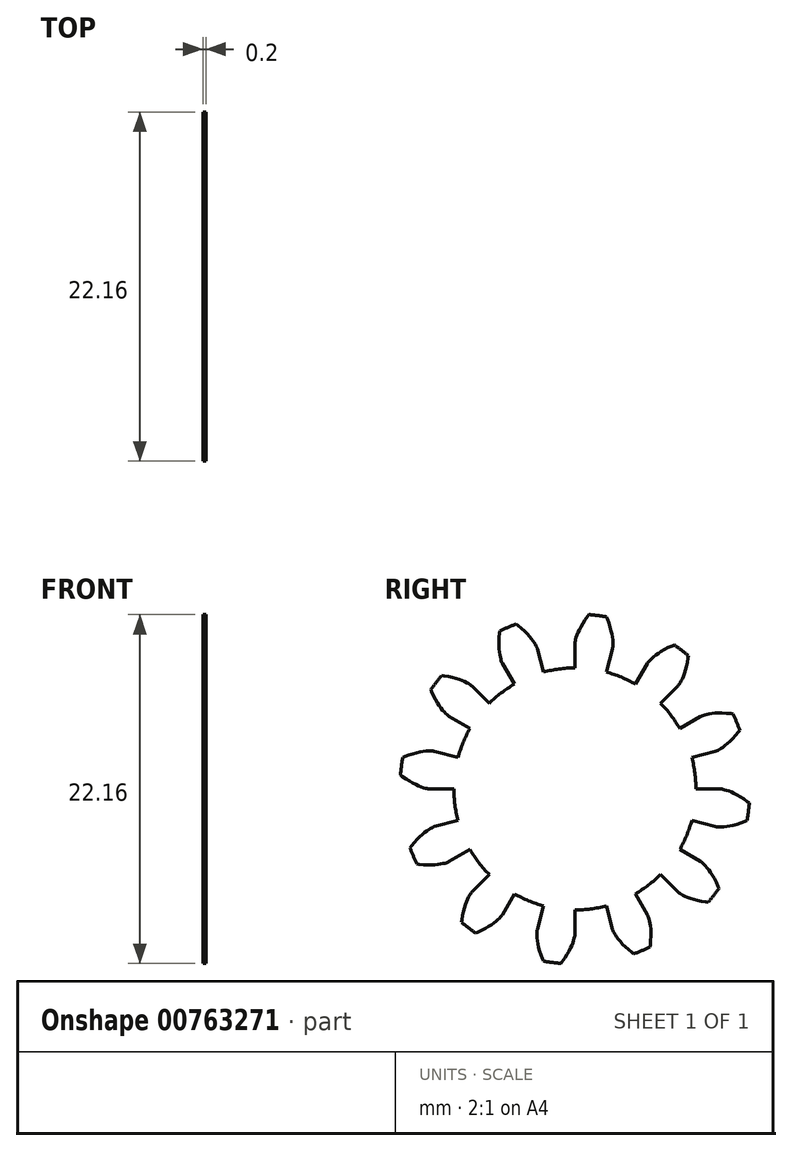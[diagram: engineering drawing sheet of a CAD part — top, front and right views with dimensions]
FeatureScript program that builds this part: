
annotation { "Feature Type Name" : "Feature", "Feature Type Description" : "" }
export const myFeature = defineFeature(function(context is Context, id is Id, definition is map)
    precondition{}
    {
        {
            assignVariable(context, id + "F0", {"name" : "GearThickness", "anyValue" : .196});
        }
        {
            var Q0;
            Q0=qCreatedBy(makeId("Right.planeOp"),FACE);
            var sketch = newSketch(context, id + "F1", { "sketchPlane" : qUnion([Q0])});
            skCircle(sketch, "E0", {"center": v(0, 0) * mm, "radius": 7.69 * mm});
            skCircle(sketch, "E1", {"center": v(0, 0) * mm, "radius": 9.22 * mm, "construction": true});
            skCircle(sketch, "E2", {"center": v(0, 0) * mm, "radius": 9.53 * mm, "construction": true});
            skCircle(sketch, "E3", {"center": v(0, 0) * mm, "radius": 11.11 * mm});
            skLineSegment(sketch, "E4", {"start": v(0, 0) * mm, "end": v(-9.22, 0) * mm, "construction": true});
            skLineSegment(sketch, "E5.1.0", {"start": v(0, 0) * mm, "end": v(-9.21, 0.46) * mm, "construction": true});
            skLineSegment(sketch, "E5.2.0", {"start": v(0, 0) * mm, "end": v(-9.18, 0.92) * mm, "construction": true});
            skLineSegment(sketch, "E5.3.0", {"start": v(0, 0) * mm, "end": v(-9.12, 1.38) * mm, "construction": true});
            skLineSegment(sketch, "E5.4.0", {"start": v(0, 0) * mm, "end": v(-9.04, 1.83) * mm, "construction": true});
            skLineSegment(sketch, "E5.5.0", {"start": v(0, 0) * mm, "end": v(-8.93, 2.28) * mm, "construction": true});
            skLineSegment(sketch, "E5.6.0", {"start": v(0, 0) * mm, "end": v(-8.8, 2.73) * mm, "construction": true});
            skLineSegment(sketch, "E5.7.0", {"start": v(0, 0) * mm, "end": v(-8.66, 3.16) * mm, "construction": true});
            skLineSegment(sketch, "E5.8.0", {"start": v(0, 0) * mm, "end": v(-8.5, 3.6) * mm, "construction": true});
            skLineSegment(sketch, "E5.9.0", {"start": v(0, 0) * mm, "end": v(-8.3, 4.01) * mm, "construction": true});
            skLineSegment(sketch, "E5.10.0", {"start": v(0, 0) * mm, "end": v(-8.1, 4.42) * mm, "construction": true});
            skLineSegment(sketch, "E5.11.0", {"start": v(0, 0) * mm, "end": v(-7.86, 4.82) * mm, "construction": true});
            skLineSegment(sketch, "E5.12.0", {"start": v(0, 0) * mm, "end": v(-7.61, 5.2) * mm, "construction": true});
            skLineSegment(sketch, "E5.13.0", {"start": v(0, 0) * mm, "end": v(-7.34, 5.58) * mm, "construction": true});
            skLineSegment(sketch, "E5.14.0", {"start": v(0, 0) * mm, "end": v(-7.05, 5.94) * mm, "construction": true});
            skLineSegment(sketch, "E5.anchor2", {"start": v(0, 0) * mm, "end": v(-7.05, 5.94) * mm, "construction": true});
            skLineSegment(sketch, "E6", {"start": v(-9.21, 0.46) * mm, "end": v(-9.23, 0) * mm, "construction": true});
            skLineSegment(sketch, "E7", {"start": v(-9.18, 0.92) * mm, "end": v(-9.27, 0) * mm, "construction": true});
            skLineSegment(sketch, "E8", {"start": v(-9.12, 1.38) * mm, "end": v(-9.32, 0.01) * mm, "construction": true});
            skLineSegment(sketch, "E9", {"start": v(-8.93, 2.28) * mm, "end": v(-9.5, 0.05) * mm, "construction": true});
            skLineSegment(sketch, "E10", {"start": v(-8.8, 2.73) * mm, "end": v(-9.63, 0.08) * mm, "construction": true});
            skLineSegment(sketch, "E11", {"start": v(-8.66, 3.16) * mm, "end": v(-9.77, 0.13) * mm, "construction": true});
            skLineSegment(sketch, "E12", {"start": v(-8.5, 3.6) * mm, "end": v(-9.93, 0.2) * mm, "construction": true});
            skLineSegment(sketch, "E13", {"start": v(-8.3, 4.01) * mm, "end": v(-10.1, 0.27) * mm, "construction": true});
            skLineSegment(sketch, "E14", {"start": v(-8.1, 4.42) * mm, "end": v(-10.3, 0.37) * mm, "construction": true});
            skLineSegment(sketch, "E15", {"start": v(-7.86, 4.82) * mm, "end": v(-10.51, 0.5) * mm, "construction": true});
            skLineSegment(sketch, "E16", {"start": v(-9.04, 1.83) * mm, "end": v(-9.4, 0.02) * mm, "construction": true});
            skLineSegment(sketch, "E17", {"start": v(-7.61, 5.2) * mm, "end": v(-10.74, 0.64) * mm, "construction": true});
            skLineSegment(sketch, "E18", {"start": v(-7.34, 5.58) * mm, "end": v(-10.97, 0.8) * mm, "construction": true});
            skLineSegment(sketch, "E19", {"start": v(-7.05, 5.94) * mm, "end": v(-11.21, 1) * mm, "construction": true});
            skLineSegment(sketch, "E20", {"start": v(0, 0) * mm, "end": v(-9.14, 1.2) * mm, "construction": true});
            skLineSegment(sketch, "E21", {"start": v(-7.69, 0) * mm, "end": v(-9.22, 0) * mm});
            skLineSegment(sketch, "E22.MirrorCS", {"start": v(-7.43, 1.99) * mm, "end": v(-8.9, 2.39) * mm});
            skLineSegment(sketch, "E23", {"start": v(-9.22, 0) * mm, "end": v(-9.23, 0) * mm});
            skLineSegment(sketch, "E24", {"start": v(-9.23, 0) * mm, "end": v(-9.27, 0) * mm});
            skLineSegment(sketch, "E25", {"start": v(-9.27, 0) * mm, "end": v(-9.32, 0.01) * mm});
            skLineSegment(sketch, "E26", {"start": v(-9.32, 0.01) * mm, "end": v(-9.4, 0.02) * mm});
            skLineSegment(sketch, "E27", {"start": v(-9.4, 0.02) * mm, "end": v(-9.5, 0.05) * mm});
            skLineSegment(sketch, "E28", {"start": v(-9.5, 0.05) * mm, "end": v(-9.63, 0.08) * mm});
            skLineSegment(sketch, "E29", {"start": v(-9.63, 0.08) * mm, "end": v(-9.77, 0.13) * mm});
            skLineSegment(sketch, "E30", {"start": v(-9.77, 0.13) * mm, "end": v(-9.93, 0.2) * mm});
            skLineSegment(sketch, "E31", {"start": v(-9.93, 0.2) * mm, "end": v(-10.1, 0.27) * mm});
            skLineSegment(sketch, "E32", {"start": v(-10.1, 0.27) * mm, "end": v(-10.3, 0.37) * mm});
            skLineSegment(sketch, "E33", {"start": v(-10.3, 0.37) * mm, "end": v(-10.51, 0.5) * mm});
            skLineSegment(sketch, "E34", {"start": v(-10.51, 0.5) * mm, "end": v(-10.74, 0.64) * mm});
            skLineSegment(sketch, "E35", {"start": v(-10.74, 0.64) * mm, "end": v(-10.97, 0.8) * mm});
            skLineSegment(sketch, "E36", {"start": v(-10.97, 0.8) * mm, "end": v(-11.21, 1) * mm});
            skLineSegment(sketch, "E37.MirrorCS", {"start": v(-8.9, 2.39) * mm, "end": v(-8.92, 2.39) * mm});
            skLineSegment(sketch, "E38.MirrorCS", {"start": v(-8.92, 2.39) * mm, "end": v(-8.95, 2.4) * mm});
            skLineSegment(sketch, "E39.MirrorCS", {"start": v(-8.95, 2.4) * mm, "end": v(-9, 2.4) * mm});
            skLineSegment(sketch, "E40.MirrorCS", {"start": v(-9, 2.4) * mm, "end": v(-9.1, 2.41) * mm});
            skLineSegment(sketch, "E41.MirrorCS", {"start": v(-9.2, 2.41) * mm, "end": v(-9.32, 2.41) * mm});
            skLineSegment(sketch, "E42.MirrorCS", {"start": v(-9.32, 2.41) * mm, "end": v(-9.47, 2.4) * mm});
            skLineSegment(sketch, "E43.MirrorCS", {"start": v(-9.47, 2.4) * mm, "end": v(-9.64, 2.38) * mm});
            skLineSegment(sketch, "E44.MirrorCS", {"start": v(-9.64, 2.38) * mm, "end": v(-9.84, 2.35) * mm});
            skLineSegment(sketch, "E45.MirrorCS", {"start": v(-10.05, 2.3) * mm, "end": v(-10.28, 2.24) * mm});
            skLineSegment(sketch, "E46.MirrorCS", {"start": v(-9.84, 2.35) * mm, "end": v(-10.05, 2.3) * mm});
            skLineSegment(sketch, "E47.MirrorCS", {"start": v(-10.28, 2.24) * mm, "end": v(-10.54, 2.16) * mm});
            skLineSegment(sketch, "E48.MirrorCS", {"start": v(-10.54, 2.16) * mm, "end": v(-10.8, 2.06) * mm});
            skLineSegment(sketch, "E49.MirrorCS", {"start": v(-10.8, 2.06) * mm, "end": v(-11.09, 1.93) * mm});
            skLineSegment(sketch, "E50.MirrorCS", {"start": v(-9.1, 2.41) * mm, "end": v(-9.2, 2.41) * mm});
            skLineSegment(sketch, "E51.1.0", {"start": v(-6.66, -3.84) * mm, "end": v(-7.99, -4.61) * mm});
            skLineSegment(sketch, "E51.1.1", {"start": v(-10.03, -3.2) * mm, "end": v(-10.2, -3.4) * mm});
            skLineSegment(sketch, "E51.1.2", {"start": v(-7.43, -1.99) * mm, "end": v(-8.9, -2.39) * mm});
            skLineSegment(sketch, "E51.1.3", {"start": v(-9.86, -3.03) * mm, "end": v(-10.03, -3.2) * mm});
            skLineSegment(sketch, "E51.1.4", {"start": v(-9.11, -4.83) * mm, "end": v(-9.35, -4.83) * mm});
            skLineSegment(sketch, "E51.1.5", {"start": v(-9.35, -4.83) * mm, "end": v(-9.62, -4.81) * mm});
            skLineSegment(sketch, "E51.1.6", {"start": v(-9.7, -2.88) * mm, "end": v(-9.86, -3.03) * mm});
            skLineSegment(sketch, "E51.1.7", {"start": v(-10.39, -3.62) * mm, "end": v(-10.57, -3.87) * mm});
            skLineSegment(sketch, "E51.1.8", {"start": v(-9.54, -2.76) * mm, "end": v(-9.7, -2.88) * mm});
            skLineSegment(sketch, "E51.1.9", {"start": v(-9.9, -4.78) * mm, "end": v(-10.21, -4.74) * mm});
            skLineSegment(sketch, "E51.1.10", {"start": v(-10.2, -3.4) * mm, "end": v(-10.39, -3.62) * mm});
            skLineSegment(sketch, "E51.1.11", {"start": v(-8.9, -4.82) * mm, "end": v(-9.11, -4.83) * mm});
            skLineSegment(sketch, "E51.1.12", {"start": v(-9.62, -4.81) * mm, "end": v(-9.9, -4.78) * mm});
            skLineSegment(sketch, "E51.1.13", {"start": v(-9.17, -2.5) * mm, "end": v(-9.28, -2.57) * mm});
            skLineSegment(sketch, "E51.1.14", {"start": v(-9.28, -2.57) * mm, "end": v(-9.4, -2.65) * mm});
            skLineSegment(sketch, "E51.1.15", {"start": v(-9.4, -2.65) * mm, "end": v(-9.54, -2.76) * mm});
            skLineSegment(sketch, "E51.1.16", {"start": v(-8.53, -4.77) * mm, "end": v(-8.7, -4.8) * mm});
            skLineSegment(sketch, "E51.1.17", {"start": v(-8.38, -4.74) * mm, "end": v(-8.53, -4.77) * mm});
            skLineSegment(sketch, "E51.1.18", {"start": v(-8.7, -4.8) * mm, "end": v(-8.9, -4.82) * mm});
            skLineSegment(sketch, "E51.1.19", {"start": v(-9.08, -2.46) * mm, "end": v(-9.17, -2.5) * mm});
            skLineSegment(sketch, "E51.1.20", {"start": v(-9, -2.42) * mm, "end": v(-9.08, -2.46) * mm});
            skLineSegment(sketch, "E51.1.21", {"start": v(-8.26, -4.71) * mm, "end": v(-8.38, -4.74) * mm});
            skLineSegment(sketch, "E51.1.22", {"start": v(-8.16, -4.68) * mm, "end": v(-8.26, -4.71) * mm});
            skLineSegment(sketch, "E51.1.23", {"start": v(-8.03, -4.63) * mm, "end": v(-8.08, -4.65) * mm});
            skLineSegment(sketch, "E51.1.24", {"start": v(-8.9, -2.39) * mm, "end": v(-8.92, -2.4) * mm});
            skLineSegment(sketch, "E51.1.25", {"start": v(-8.92, -2.4) * mm, "end": v(-8.95, -2.4) * mm});
            skLineSegment(sketch, "E51.1.26", {"start": v(-8.08, -4.65) * mm, "end": v(-8.16, -4.68) * mm});
            skLineSegment(sketch, "E51.1.27", {"start": v(-8.95, -2.4) * mm, "end": v(-9, -2.42) * mm});
            skLineSegment(sketch, "E51.1.28", {"start": v(-8, -4.62) * mm, "end": v(-8.03, -4.63) * mm});
            skLineSegment(sketch, "E51.1.29", {"start": v(-7.99, -4.61) * mm, "end": v(-8, -4.62) * mm});
            skLineSegment(sketch, "E51.2.0", {"start": v(-3.84, -6.66) * mm, "end": v(-4.61, -7.99) * mm});
            skLineSegment(sketch, "E51.2.1", {"start": v(-7.08, -7.78) * mm, "end": v(-7.14, -8.04) * mm});
            skLineSegment(sketch, "E51.2.2", {"start": v(-5.44, -5.44) * mm, "end": v(-6.52, -6.52) * mm});
            skLineSegment(sketch, "E51.2.3", {"start": v(-7.02, -7.55) * mm, "end": v(-7.08, -7.78) * mm});
            skLineSegment(sketch, "E51.2.4", {"start": v(-5.48, -8.74) * mm, "end": v(-5.69, -8.86) * mm});
            skLineSegment(sketch, "E51.2.5", {"start": v(-5.69, -8.86) * mm, "end": v(-5.92, -8.98) * mm});
            skLineSegment(sketch, "E51.2.6", {"start": v(-6.95, -7.34) * mm, "end": v(-7.02, -7.55) * mm});
            skLineSegment(sketch, "E51.2.7", {"start": v(-7.18, -8.33) * mm, "end": v(-7.22, -8.64) * mm});
            skLineSegment(sketch, "E51.2.8", {"start": v(-6.88, -7.16) * mm, "end": v(-6.95, -7.34) * mm});
            skLineSegment(sketch, "E51.2.9", {"start": v(-6.18, -9.1) * mm, "end": v(-6.47, -9.2) * mm});
            skLineSegment(sketch, "E51.2.10", {"start": v(-7.14, -8.04) * mm, "end": v(-7.18, -8.33) * mm});
            skLineSegment(sketch, "E51.2.11", {"start": v(-5.3, -8.62) * mm, "end": v(-5.48, -8.74) * mm});
            skLineSegment(sketch, "E51.2.12", {"start": v(-5.92, -8.98) * mm, "end": v(-6.18, -9.1) * mm});
            skLineSegment(sketch, "E51.2.13", {"start": v(-6.69, -6.76) * mm, "end": v(-6.75, -6.87) * mm});
            skLineSegment(sketch, "E51.2.14", {"start": v(-6.75, -6.87) * mm, "end": v(-6.82, -7) * mm});
            skLineSegment(sketch, "E51.2.15", {"start": v(-6.82, -7) * mm, "end": v(-6.88, -7.16) * mm});
            skLineSegment(sketch, "E51.2.16", {"start": v(-5, -8.4) * mm, "end": v(-5.13, -8.5) * mm});
            skLineSegment(sketch, "E51.2.17", {"start": v(-4.88, -8.3) * mm, "end": v(-5, -8.4) * mm});
            skLineSegment(sketch, "E51.2.18", {"start": v(-5.13, -8.5) * mm, "end": v(-5.3, -8.62) * mm});
            skLineSegment(sketch, "E51.2.19", {"start": v(-6.63, -6.67) * mm, "end": v(-6.69, -6.76) * mm});
            skLineSegment(sketch, "E51.2.20", {"start": v(-6.59, -6.6) * mm, "end": v(-6.63, -6.67) * mm});
            skLineSegment(sketch, "E51.2.21", {"start": v(-4.8, -8.2) * mm, "end": v(-4.88, -8.3) * mm});
            skLineSegment(sketch, "E51.2.22", {"start": v(-4.72, -8.13) * mm, "end": v(-4.8, -8.2) * mm});
            skLineSegment(sketch, "E51.2.23", {"start": v(-4.64, -8.02) * mm, "end": v(-4.67, -8.07) * mm});
            skLineSegment(sketch, "E51.2.24", {"start": v(-6.52, -6.52) * mm, "end": v(-6.53, -6.53) * mm});
            skLineSegment(sketch, "E51.2.25", {"start": v(-6.53, -6.53) * mm, "end": v(-6.55, -6.56) * mm});
            skLineSegment(sketch, "E51.2.26", {"start": v(-4.67, -8.07) * mm, "end": v(-4.72, -8.13) * mm});
            skLineSegment(sketch, "E51.2.27", {"start": v(-6.55, -6.56) * mm, "end": v(-6.59, -6.6) * mm});
            skLineSegment(sketch, "E51.2.28", {"start": v(-4.62, -8) * mm, "end": v(-4.64, -8.02) * mm});
            skLineSegment(sketch, "E51.2.29", {"start": v(-4.61, -7.99) * mm, "end": v(-4.62, -8) * mm});
            skLineSegment(sketch, "E51.3.0", {"start": v(0, -7.69) * mm, "end": v(0, -9.22) * mm});
            skLineSegment(sketch, "E51.3.1", {"start": v(-2.24, -10.28) * mm, "end": v(-2.16, -10.54) * mm});
            skLineSegment(sketch, "E51.3.2", {"start": v(-1.99, -7.43) * mm, "end": v(-2.39, -8.9) * mm});
            skLineSegment(sketch, "E51.3.3", {"start": v(-2.3, -10.05) * mm, "end": v(-2.24, -10.28) * mm});
            skLineSegment(sketch, "E51.3.4", {"start": v(-0.37, -10.3) * mm, "end": v(-0.5, -10.51) * mm});
            skLineSegment(sketch, "E51.3.5", {"start": v(-0.5, -10.51) * mm, "end": v(-0.64, -10.74) * mm});
            skLineSegment(sketch, "E51.3.6", {"start": v(-2.35, -9.84) * mm, "end": v(-2.3, -10.05) * mm});
            skLineSegment(sketch, "E51.3.7", {"start": v(-2.06, -10.8) * mm, "end": v(-1.93, -11.09) * mm});
            skLineSegment(sketch, "E51.3.8", {"start": v(-2.38, -9.64) * mm, "end": v(-2.35, -9.84) * mm});
            skLineSegment(sketch, "E51.3.9", {"start": v(-0.8, -10.97) * mm, "end": v(-1, -11.21) * mm});
            skLineSegment(sketch, "E51.3.10", {"start": v(-2.16, -10.54) * mm, "end": v(-2.06, -10.8) * mm});
            skLineSegment(sketch, "E51.3.11", {"start": v(-0.27, -10.1) * mm, "end": v(-0.37, -10.3) * mm});
            skLineSegment(sketch, "E51.3.12", {"start": v(-0.64, -10.74) * mm, "end": v(-0.8, -10.97) * mm});
            skLineSegment(sketch, "E51.3.13", {"start": v(-2.41, -9.2) * mm, "end": v(-2.41, -9.32) * mm});
            skLineSegment(sketch, "E51.3.14", {"start": v(-2.41, -9.32) * mm, "end": v(-2.4, -9.47) * mm});
            skLineSegment(sketch, "E51.3.15", {"start": v(-2.4, -9.47) * mm, "end": v(-2.38, -9.64) * mm});
            skLineSegment(sketch, "E51.3.16", {"start": v(-0.13, -9.77) * mm, "end": v(-0.2, -9.93) * mm});
            skLineSegment(sketch, "E51.3.17", {"start": v(-0.08, -9.63) * mm, "end": v(-0.13, -9.77) * mm});
            skLineSegment(sketch, "E51.3.18", {"start": v(-0.2, -9.93) * mm, "end": v(-0.27, -10.1) * mm});
            skLineSegment(sketch, "E51.3.19", {"start": v(-2.41, -9.1) * mm, "end": v(-2.41, -9.2) * mm});
            skLineSegment(sketch, "E51.3.20", {"start": v(-2.4, -9) * mm, "end": v(-2.41, -9.1) * mm});
            skLineSegment(sketch, "E51.3.21", {"start": v(-0.05, -9.5) * mm, "end": v(-0.08, -9.63) * mm});
            skLineSegment(sketch, "E51.3.22", {"start": v(-0.02, -9.4) * mm, "end": v(-0.05, -9.5) * mm});
            skLineSegment(sketch, "E51.3.23", {"start": v(0, -9.27) * mm, "end": v(-0.01, -9.32) * mm});
            skLineSegment(sketch, "E51.3.24", {"start": v(-2.39, -8.9) * mm, "end": v(-2.39, -8.92) * mm});
            skLineSegment(sketch, "E51.3.25", {"start": v(-2.39, -8.92) * mm, "end": v(-2.4, -8.95) * mm});
            skLineSegment(sketch, "E51.3.26", {"start": v(-0.01, -9.32) * mm, "end": v(-0.02, -9.4) * mm});
            skLineSegment(sketch, "E51.3.27", {"start": v(-2.4, -8.95) * mm, "end": v(-2.4, -9) * mm});
            skLineSegment(sketch, "E51.3.28", {"start": v(0, -9.23) * mm, "end": v(0, -9.27) * mm});
            skLineSegment(sketch, "E51.3.29", {"start": v(0, -9.22) * mm, "end": v(0, -9.23) * mm});
            skLineSegment(sketch, "E51.4.0", {"start": v(3.84, -6.66) * mm, "end": v(4.61, -7.99) * mm});
            skLineSegment(sketch, "E51.4.1", {"start": v(3.2, -10.03) * mm, "end": v(3.4, -10.2) * mm});
            skLineSegment(sketch, "E51.4.2", {"start": v(1.99, -7.43) * mm, "end": v(2.39, -8.9) * mm});
            skLineSegment(sketch, "E51.4.3", {"start": v(3.03, -9.86) * mm, "end": v(3.2, -10.03) * mm});
            skLineSegment(sketch, "E51.4.4", {"start": v(4.83, -9.11) * mm, "end": v(4.83, -9.35) * mm});
            skLineSegment(sketch, "E51.4.5", {"start": v(4.83, -9.35) * mm, "end": v(4.81, -9.62) * mm});
            skLineSegment(sketch, "E51.4.6", {"start": v(2.88, -9.7) * mm, "end": v(3.03, -9.86) * mm});
            skLineSegment(sketch, "E51.4.7", {"start": v(3.62, -10.39) * mm, "end": v(3.87, -10.57) * mm});
            skLineSegment(sketch, "E51.4.8", {"start": v(2.76, -9.54) * mm, "end": v(2.88, -9.7) * mm});
            skLineSegment(sketch, "E51.4.9", {"start": v(4.78, -9.9) * mm, "end": v(4.74, -10.21) * mm});
            skLineSegment(sketch, "E51.4.10", {"start": v(3.4, -10.2) * mm, "end": v(3.62, -10.39) * mm});
            skLineSegment(sketch, "E51.4.11", {"start": v(4.82, -8.9) * mm, "end": v(4.83, -9.11) * mm});
            skLineSegment(sketch, "E51.4.12", {"start": v(4.81, -9.62) * mm, "end": v(4.78, -9.9) * mm});
            skLineSegment(sketch, "E51.4.13", {"start": v(2.5, -9.17) * mm, "end": v(2.57, -9.28) * mm});
            skLineSegment(sketch, "E51.4.14", {"start": v(2.57, -9.28) * mm, "end": v(2.65, -9.4) * mm});
            skLineSegment(sketch, "E51.4.15", {"start": v(2.65, -9.4) * mm, "end": v(2.76, -9.54) * mm});
            skLineSegment(sketch, "E51.4.16", {"start": v(4.77, -8.53) * mm, "end": v(4.8, -8.7) * mm});
            skLineSegment(sketch, "E51.4.17", {"start": v(4.74, -8.38) * mm, "end": v(4.77, -8.53) * mm});
            skLineSegment(sketch, "E51.4.18", {"start": v(4.8, -8.7) * mm, "end": v(4.82, -8.9) * mm});
            skLineSegment(sketch, "E51.4.19", {"start": v(2.46, -9.08) * mm, "end": v(2.5, -9.17) * mm});
            skLineSegment(sketch, "E51.4.20", {"start": v(2.42, -9) * mm, "end": v(2.46, -9.08) * mm});
            skLineSegment(sketch, "E51.4.21", {"start": v(4.71, -8.26) * mm, "end": v(4.74, -8.38) * mm});
            skLineSegment(sketch, "E51.4.22", {"start": v(4.68, -8.16) * mm, "end": v(4.71, -8.26) * mm});
            skLineSegment(sketch, "E51.4.23", {"start": v(4.63, -8.03) * mm, "end": v(4.65, -8.08) * mm});
            skLineSegment(sketch, "E51.4.24", {"start": v(2.39, -8.9) * mm, "end": v(2.4, -8.92) * mm});
            skLineSegment(sketch, "E51.4.25", {"start": v(2.4, -8.92) * mm, "end": v(2.4, -8.95) * mm});
            skLineSegment(sketch, "E51.4.26", {"start": v(4.65, -8.08) * mm, "end": v(4.68, -8.16) * mm});
            skLineSegment(sketch, "E51.4.27", {"start": v(2.4, -8.95) * mm, "end": v(2.42, -9) * mm});
            skLineSegment(sketch, "E51.4.28", {"start": v(4.62, -8) * mm, "end": v(4.63, -8.03) * mm});
            skLineSegment(sketch, "E51.4.29", {"start": v(4.61, -7.99) * mm, "end": v(4.62, -8) * mm});
            skLineSegment(sketch, "E51.5.0", {"start": v(6.66, -3.84) * mm, "end": v(7.99, -4.61) * mm});
            skLineSegment(sketch, "E51.5.1", {"start": v(7.78, -7.08) * mm, "end": v(8.04, -7.14) * mm});
            skLineSegment(sketch, "E51.5.2", {"start": v(5.44, -5.44) * mm, "end": v(6.52, -6.52) * mm});
            skLineSegment(sketch, "E51.5.3", {"start": v(7.55, -7.02) * mm, "end": v(7.78, -7.08) * mm});
            skLineSegment(sketch, "E51.5.4", {"start": v(8.74, -5.48) * mm, "end": v(8.86, -5.69) * mm});
            skLineSegment(sketch, "E51.5.5", {"start": v(8.86, -5.69) * mm, "end": v(8.98, -5.92) * mm});
            skLineSegment(sketch, "E51.5.6", {"start": v(7.34, -6.95) * mm, "end": v(7.55, -7.02) * mm});
            skLineSegment(sketch, "E51.5.7", {"start": v(8.33, -7.18) * mm, "end": v(8.64, -7.22) * mm});
            skLineSegment(sketch, "E51.5.8", {"start": v(7.16, -6.88) * mm, "end": v(7.34, -6.95) * mm});
            skLineSegment(sketch, "E51.5.9", {"start": v(9.1, -6.18) * mm, "end": v(9.2, -6.47) * mm});
            skLineSegment(sketch, "E51.5.10", {"start": v(8.04, -7.14) * mm, "end": v(8.33, -7.18) * mm});
            skLineSegment(sketch, "E51.5.11", {"start": v(8.62, -5.3) * mm, "end": v(8.74, -5.48) * mm});
            skLineSegment(sketch, "E51.5.12", {"start": v(8.98, -5.92) * mm, "end": v(9.1, -6.18) * mm});
            skLineSegment(sketch, "E51.5.13", {"start": v(6.76, -6.69) * mm, "end": v(6.87, -6.75) * mm});
            skLineSegment(sketch, "E51.5.14", {"start": v(6.87, -6.75) * mm, "end": v(7, -6.82) * mm});
            skLineSegment(sketch, "E51.5.15", {"start": v(7, -6.82) * mm, "end": v(7.16, -6.88) * mm});
            skLineSegment(sketch, "E51.5.16", {"start": v(8.4, -5) * mm, "end": v(8.5, -5.13) * mm});
            skLineSegment(sketch, "E51.5.17", {"start": v(8.3, -4.88) * mm, "end": v(8.4, -5) * mm});
            skLineSegment(sketch, "E51.5.18", {"start": v(8.5, -5.13) * mm, "end": v(8.62, -5.3) * mm});
            skLineSegment(sketch, "E51.5.19", {"start": v(6.67, -6.63) * mm, "end": v(6.76, -6.69) * mm});
            skLineSegment(sketch, "E51.5.20", {"start": v(6.6, -6.59) * mm, "end": v(6.67, -6.63) * mm});
            skLineSegment(sketch, "E51.5.21", {"start": v(8.2, -4.8) * mm, "end": v(8.3, -4.88) * mm});
            skLineSegment(sketch, "E51.5.22", {"start": v(8.13, -4.72) * mm, "end": v(8.2, -4.8) * mm});
            skLineSegment(sketch, "E51.5.23", {"start": v(8.02, -4.64) * mm, "end": v(8.07, -4.67) * mm});
            skLineSegment(sketch, "E51.5.24", {"start": v(6.52, -6.52) * mm, "end": v(6.53, -6.53) * mm});
            skLineSegment(sketch, "E51.5.25", {"start": v(6.53, -6.53) * mm, "end": v(6.56, -6.55) * mm});
            skLineSegment(sketch, "E51.5.26", {"start": v(8.07, -4.67) * mm, "end": v(8.13, -4.72) * mm});
            skLineSegment(sketch, "E51.5.27", {"start": v(6.56, -6.55) * mm, "end": v(6.6, -6.59) * mm});
            skLineSegment(sketch, "E51.5.28", {"start": v(8, -4.62) * mm, "end": v(8.02, -4.64) * mm});
            skLineSegment(sketch, "E51.5.29", {"start": v(7.99, -4.61) * mm, "end": v(8, -4.62) * mm});
            skLineSegment(sketch, "E51.6.0", {"start": v(7.69, 0) * mm, "end": v(9.22, 0) * mm});
            skLineSegment(sketch, "E51.6.1", {"start": v(10.28, -2.24) * mm, "end": v(10.54, -2.16) * mm});
            skLineSegment(sketch, "E51.6.2", {"start": v(7.43, -1.99) * mm, "end": v(8.9, -2.39) * mm});
            skLineSegment(sketch, "E51.6.3", {"start": v(10.05, -2.3) * mm, "end": v(10.28, -2.24) * mm});
            skLineSegment(sketch, "E51.6.4", {"start": v(10.3, -0.37) * mm, "end": v(10.51, -0.5) * mm});
            skLineSegment(sketch, "E51.6.5", {"start": v(10.51, -0.5) * mm, "end": v(10.74, -0.64) * mm});
            skLineSegment(sketch, "E51.6.6", {"start": v(9.84, -2.35) * mm, "end": v(10.05, -2.3) * mm});
            skLineSegment(sketch, "E51.6.7", {"start": v(10.8, -2.06) * mm, "end": v(11.09, -1.93) * mm});
            skLineSegment(sketch, "E51.6.8", {"start": v(9.64, -2.38) * mm, "end": v(9.84, -2.35) * mm});
            skLineSegment(sketch, "E51.6.9", {"start": v(10.97, -0.8) * mm, "end": v(11.21, -1) * mm});
            skLineSegment(sketch, "E51.6.10", {"start": v(10.54, -2.16) * mm, "end": v(10.8, -2.06) * mm});
            skLineSegment(sketch, "E51.6.11", {"start": v(10.1, -0.27) * mm, "end": v(10.3, -0.37) * mm});
            skLineSegment(sketch, "E51.6.12", {"start": v(10.74, -0.64) * mm, "end": v(10.97, -0.8) * mm});
            skLineSegment(sketch, "E51.6.13", {"start": v(9.2, -2.41) * mm, "end": v(9.32, -2.41) * mm});
            skLineSegment(sketch, "E51.6.14", {"start": v(9.32, -2.41) * mm, "end": v(9.47, -2.4) * mm});
            skLineSegment(sketch, "E51.6.15", {"start": v(9.47, -2.4) * mm, "end": v(9.64, -2.38) * mm});
            skLineSegment(sketch, "E51.6.16", {"start": v(9.77, -0.13) * mm, "end": v(9.93, -0.2) * mm});
            skLineSegment(sketch, "E51.6.17", {"start": v(9.63, -0.08) * mm, "end": v(9.77, -0.13) * mm});
            skLineSegment(sketch, "E51.6.18", {"start": v(9.93, -0.2) * mm, "end": v(10.1, -0.27) * mm});
            skLineSegment(sketch, "E51.6.19", {"start": v(9.1, -2.41) * mm, "end": v(9.2, -2.41) * mm});
            skLineSegment(sketch, "E51.6.20", {"start": v(9, -2.4) * mm, "end": v(9.1, -2.41) * mm});
            skLineSegment(sketch, "E51.6.21", {"start": v(9.5, -0.05) * mm, "end": v(9.63, -0.08) * mm});
            skLineSegment(sketch, "E51.6.22", {"start": v(9.4, -0.02) * mm, "end": v(9.5, -0.05) * mm});
            skLineSegment(sketch, "E51.6.23", {"start": v(9.27, 0) * mm, "end": v(9.32, -0.01) * mm});
            skLineSegment(sketch, "E51.6.24", {"start": v(8.9, -2.39) * mm, "end": v(8.92, -2.39) * mm});
            skLineSegment(sketch, "E51.6.25", {"start": v(8.92, -2.39) * mm, "end": v(8.95, -2.4) * mm});
            skLineSegment(sketch, "E51.6.26", {"start": v(9.32, -0.01) * mm, "end": v(9.4, -0.02) * mm});
            skLineSegment(sketch, "E51.6.27", {"start": v(8.95, -2.4) * mm, "end": v(9, -2.4) * mm});
            skLineSegment(sketch, "E51.6.28", {"start": v(9.23, 0) * mm, "end": v(9.27, 0) * mm});
            skLineSegment(sketch, "E51.6.29", {"start": v(9.22, 0) * mm, "end": v(9.23, 0) * mm});
            skLineSegment(sketch, "E51.7.0", {"start": v(6.66, 3.84) * mm, "end": v(7.99, 4.61) * mm});
            skLineSegment(sketch, "E51.7.1", {"start": v(10.03, 3.2) * mm, "end": v(10.2, 3.4) * mm});
            skLineSegment(sketch, "E51.7.2", {"start": v(7.43, 1.99) * mm, "end": v(8.9, 2.39) * mm});
            skLineSegment(sketch, "E51.7.3", {"start": v(9.86, 3.03) * mm, "end": v(10.03, 3.2) * mm});
            skLineSegment(sketch, "E51.7.4", {"start": v(9.11, 4.83) * mm, "end": v(9.35, 4.83) * mm});
            skLineSegment(sketch, "E51.7.5", {"start": v(9.35, 4.83) * mm, "end": v(9.62, 4.81) * mm});
            skLineSegment(sketch, "E51.7.6", {"start": v(9.7, 2.88) * mm, "end": v(9.86, 3.03) * mm});
            skLineSegment(sketch, "E51.7.7", {"start": v(10.39, 3.62) * mm, "end": v(10.57, 3.87) * mm});
            skLineSegment(sketch, "E51.7.8", {"start": v(9.54, 2.76) * mm, "end": v(9.7, 2.88) * mm});
            skLineSegment(sketch, "E51.7.9", {"start": v(9.9, 4.78) * mm, "end": v(10.21, 4.74) * mm});
            skLineSegment(sketch, "E51.7.10", {"start": v(10.2, 3.4) * mm, "end": v(10.39, 3.62) * mm});
            skLineSegment(sketch, "E51.7.11", {"start": v(8.9, 4.82) * mm, "end": v(9.11, 4.83) * mm});
            skLineSegment(sketch, "E51.7.12", {"start": v(9.62, 4.81) * mm, "end": v(9.9, 4.78) * mm});
            skLineSegment(sketch, "E51.7.13", {"start": v(9.17, 2.5) * mm, "end": v(9.28, 2.57) * mm});
            skLineSegment(sketch, "E51.7.14", {"start": v(9.28, 2.57) * mm, "end": v(9.4, 2.65) * mm});
            skLineSegment(sketch, "E51.7.15", {"start": v(9.4, 2.65) * mm, "end": v(9.54, 2.76) * mm});
            skLineSegment(sketch, "E51.7.16", {"start": v(8.53, 4.77) * mm, "end": v(8.7, 4.8) * mm});
            skLineSegment(sketch, "E51.7.17", {"start": v(8.38, 4.74) * mm, "end": v(8.53, 4.77) * mm});
            skLineSegment(sketch, "E51.7.18", {"start": v(8.7, 4.8) * mm, "end": v(8.9, 4.82) * mm});
            skLineSegment(sketch, "E51.7.19", {"start": v(9.08, 2.46) * mm, "end": v(9.17, 2.5) * mm});
            skLineSegment(sketch, "E51.7.20", {"start": v(9, 2.42) * mm, "end": v(9.08, 2.46) * mm});
            skLineSegment(sketch, "E51.7.21", {"start": v(8.26, 4.71) * mm, "end": v(8.38, 4.74) * mm});
            skLineSegment(sketch, "E51.7.22", {"start": v(8.16, 4.68) * mm, "end": v(8.26, 4.71) * mm});
            skLineSegment(sketch, "E51.7.23", {"start": v(8.03, 4.63) * mm, "end": v(8.08, 4.65) * mm});
            skLineSegment(sketch, "E51.7.24", {"start": v(8.9, 2.39) * mm, "end": v(8.92, 2.4) * mm});
            skLineSegment(sketch, "E51.7.25", {"start": v(8.92, 2.4) * mm, "end": v(8.95, 2.4) * mm});
            skLineSegment(sketch, "E51.7.26", {"start": v(8.08, 4.65) * mm, "end": v(8.16, 4.68) * mm});
            skLineSegment(sketch, "E51.7.27", {"start": v(8.95, 2.4) * mm, "end": v(9, 2.42) * mm});
            skLineSegment(sketch, "E51.7.28", {"start": v(8, 4.62) * mm, "end": v(8.03, 4.63) * mm});
            skLineSegment(sketch, "E51.7.29", {"start": v(7.99, 4.61) * mm, "end": v(8, 4.62) * mm});
            skLineSegment(sketch, "E51.8.0", {"start": v(3.84, 6.66) * mm, "end": v(4.61, 7.99) * mm});
            skLineSegment(sketch, "E51.8.1", {"start": v(7.08, 7.78) * mm, "end": v(7.14, 8.04) * mm});
            skLineSegment(sketch, "E51.8.2", {"start": v(5.44, 5.44) * mm, "end": v(6.52, 6.52) * mm});
            skLineSegment(sketch, "E51.8.3", {"start": v(7.02, 7.55) * mm, "end": v(7.08, 7.78) * mm});
            skLineSegment(sketch, "E51.8.4", {"start": v(5.48, 8.74) * mm, "end": v(5.69, 8.86) * mm});
            skLineSegment(sketch, "E51.8.5", {"start": v(5.69, 8.86) * mm, "end": v(5.92, 8.98) * mm});
            skLineSegment(sketch, "E51.8.6", {"start": v(6.95, 7.34) * mm, "end": v(7.02, 7.55) * mm});
            skLineSegment(sketch, "E51.8.7", {"start": v(7.18, 8.33) * mm, "end": v(7.22, 8.64) * mm});
            skLineSegment(sketch, "E51.8.8", {"start": v(6.88, 7.16) * mm, "end": v(6.95, 7.34) * mm});
            skLineSegment(sketch, "E51.8.9", {"start": v(6.18, 9.1) * mm, "end": v(6.47, 9.2) * mm});
            skLineSegment(sketch, "E51.8.10", {"start": v(7.14, 8.04) * mm, "end": v(7.18, 8.33) * mm});
            skLineSegment(sketch, "E51.8.11", {"start": v(5.3, 8.62) * mm, "end": v(5.48, 8.74) * mm});
            skLineSegment(sketch, "E51.8.12", {"start": v(5.92, 8.98) * mm, "end": v(6.18, 9.1) * mm});
            skLineSegment(sketch, "E51.8.13", {"start": v(6.69, 6.76) * mm, "end": v(6.75, 6.87) * mm});
            skLineSegment(sketch, "E51.8.14", {"start": v(6.75, 6.87) * mm, "end": v(6.82, 7) * mm});
            skLineSegment(sketch, "E51.8.15", {"start": v(6.82, 7) * mm, "end": v(6.88, 7.16) * mm});
            skLineSegment(sketch, "E51.8.16", {"start": v(5, 8.4) * mm, "end": v(5.13, 8.5) * mm});
            skLineSegment(sketch, "E51.8.17", {"start": v(4.88, 8.3) * mm, "end": v(5, 8.4) * mm});
            skLineSegment(sketch, "E51.8.18", {"start": v(5.13, 8.5) * mm, "end": v(5.3, 8.62) * mm});
            skLineSegment(sketch, "E51.8.19", {"start": v(6.63, 6.67) * mm, "end": v(6.69, 6.76) * mm});
            skLineSegment(sketch, "E51.8.20", {"start": v(6.59, 6.6) * mm, "end": v(6.63, 6.67) * mm});
            skLineSegment(sketch, "E51.8.21", {"start": v(4.8, 8.2) * mm, "end": v(4.88, 8.3) * mm});
            skLineSegment(sketch, "E51.8.22", {"start": v(4.72, 8.13) * mm, "end": v(4.8, 8.2) * mm});
            skLineSegment(sketch, "E51.8.23", {"start": v(4.64, 8.02) * mm, "end": v(4.67, 8.07) * mm});
            skLineSegment(sketch, "E51.8.24", {"start": v(6.52, 6.52) * mm, "end": v(6.53, 6.53) * mm});
            skLineSegment(sketch, "E51.8.25", {"start": v(6.53, 6.53) * mm, "end": v(6.55, 6.56) * mm});
            skLineSegment(sketch, "E51.8.26", {"start": v(4.67, 8.07) * mm, "end": v(4.72, 8.13) * mm});
            skLineSegment(sketch, "E51.8.27", {"start": v(6.55, 6.56) * mm, "end": v(6.59, 6.6) * mm});
            skLineSegment(sketch, "E51.8.28", {"start": v(4.62, 8) * mm, "end": v(4.64, 8.02) * mm});
            skLineSegment(sketch, "E51.8.29", {"start": v(4.61, 7.99) * mm, "end": v(4.62, 8) * mm});
            skLineSegment(sketch, "E51.9.0", {"start": v(0, 7.69) * mm, "end": v(0, 9.22) * mm});
            skLineSegment(sketch, "E51.9.1", {"start": v(2.24, 10.28) * mm, "end": v(2.16, 10.54) * mm});
            skLineSegment(sketch, "E51.9.2", {"start": v(1.99, 7.43) * mm, "end": v(2.39, 8.9) * mm});
            skLineSegment(sketch, "E51.9.3", {"start": v(2.3, 10.05) * mm, "end": v(2.24, 10.28) * mm});
            skLineSegment(sketch, "E51.9.4", {"start": v(0.37, 10.3) * mm, "end": v(0.5, 10.51) * mm});
            skLineSegment(sketch, "E51.9.5", {"start": v(0.5, 10.51) * mm, "end": v(0.64, 10.74) * mm});
            skLineSegment(sketch, "E51.9.6", {"start": v(2.35, 9.84) * mm, "end": v(2.3, 10.05) * mm});
            skLineSegment(sketch, "E51.9.7", {"start": v(2.06, 10.8) * mm, "end": v(1.93, 11.09) * mm});
            skLineSegment(sketch, "E51.9.8", {"start": v(2.38, 9.64) * mm, "end": v(2.35, 9.84) * mm});
            skLineSegment(sketch, "E51.9.9", {"start": v(0.8, 10.97) * mm, "end": v(1, 11.21) * mm});
            skLineSegment(sketch, "E51.9.10", {"start": v(2.16, 10.54) * mm, "end": v(2.06, 10.8) * mm});
            skLineSegment(sketch, "E51.9.11", {"start": v(0.27, 10.1) * mm, "end": v(0.37, 10.3) * mm});
            skLineSegment(sketch, "E51.9.12", {"start": v(0.64, 10.74) * mm, "end": v(0.8, 10.97) * mm});
            skLineSegment(sketch, "E51.9.13", {"start": v(2.41, 9.2) * mm, "end": v(2.41, 9.32) * mm});
            skLineSegment(sketch, "E51.9.14", {"start": v(2.41, 9.32) * mm, "end": v(2.4, 9.47) * mm});
            skLineSegment(sketch, "E51.9.15", {"start": v(2.4, 9.47) * mm, "end": v(2.38, 9.64) * mm});
            skLineSegment(sketch, "E51.9.16", {"start": v(0.13, 9.77) * mm, "end": v(0.2, 9.93) * mm});
            skLineSegment(sketch, "E51.9.17", {"start": v(0.08, 9.63) * mm, "end": v(0.13, 9.77) * mm});
            skLineSegment(sketch, "E51.9.18", {"start": v(0.2, 9.93) * mm, "end": v(0.27, 10.1) * mm});
            skLineSegment(sketch, "E51.9.19", {"start": v(2.41, 9.1) * mm, "end": v(2.41, 9.2) * mm});
            skLineSegment(sketch, "E51.9.20", {"start": v(2.4, 9) * mm, "end": v(2.41, 9.1) * mm});
            skLineSegment(sketch, "E51.9.21", {"start": v(0.05, 9.5) * mm, "end": v(0.08, 9.63) * mm});
            skLineSegment(sketch, "E51.9.22", {"start": v(0.02, 9.4) * mm, "end": v(0.05, 9.5) * mm});
            skLineSegment(sketch, "E51.9.23", {"start": v(0, 9.27) * mm, "end": v(0.01, 9.32) * mm});
            skLineSegment(sketch, "E51.9.24", {"start": v(2.39, 8.9) * mm, "end": v(2.39, 8.92) * mm});
            skLineSegment(sketch, "E51.9.25", {"start": v(2.39, 8.92) * mm, "end": v(2.4, 8.95) * mm});
            skLineSegment(sketch, "E51.9.26", {"start": v(0.01, 9.32) * mm, "end": v(0.02, 9.4) * mm});
            skLineSegment(sketch, "E51.9.27", {"start": v(2.4, 8.95) * mm, "end": v(2.4, 9) * mm});
            skLineSegment(sketch, "E51.9.28", {"start": v(0, 9.23) * mm, "end": v(0, 9.27) * mm});
            skLineSegment(sketch, "E51.9.29", {"start": v(0, 9.22) * mm, "end": v(0, 9.23) * mm});
            skLineSegment(sketch, "E51.10.0", {"start": v(-3.84, 6.66) * mm, "end": v(-4.61, 7.99) * mm});
            skLineSegment(sketch, "E51.10.1", {"start": v(-3.2, 10.03) * mm, "end": v(-3.4, 10.2) * mm});
            skLineSegment(sketch, "E51.10.2", {"start": v(-1.99, 7.43) * mm, "end": v(-2.39, 8.9) * mm});
            skLineSegment(sketch, "E51.10.3", {"start": v(-3.03, 9.86) * mm, "end": v(-3.2, 10.03) * mm});
            skLineSegment(sketch, "E51.10.4", {"start": v(-4.83, 9.11) * mm, "end": v(-4.83, 9.35) * mm});
            skLineSegment(sketch, "E51.10.5", {"start": v(-4.83, 9.35) * mm, "end": v(-4.81, 9.62) * mm});
            skLineSegment(sketch, "E51.10.6", {"start": v(-2.88, 9.7) * mm, "end": v(-3.03, 9.86) * mm});
            skLineSegment(sketch, "E51.10.7", {"start": v(-3.62, 10.39) * mm, "end": v(-3.87, 10.57) * mm});
            skLineSegment(sketch, "E51.10.8", {"start": v(-2.76, 9.54) * mm, "end": v(-2.88, 9.7) * mm});
            skLineSegment(sketch, "E51.10.9", {"start": v(-4.78, 9.9) * mm, "end": v(-4.74, 10.21) * mm});
            skLineSegment(sketch, "E51.10.10", {"start": v(-3.4, 10.2) * mm, "end": v(-3.62, 10.39) * mm});
            skLineSegment(sketch, "E51.10.11", {"start": v(-4.82, 8.9) * mm, "end": v(-4.83, 9.11) * mm});
            skLineSegment(sketch, "E51.10.12", {"start": v(-4.81, 9.62) * mm, "end": v(-4.78, 9.9) * mm});
            skLineSegment(sketch, "E51.10.13", {"start": v(-2.5, 9.17) * mm, "end": v(-2.57, 9.28) * mm});
            skLineSegment(sketch, "E51.10.14", {"start": v(-2.57, 9.28) * mm, "end": v(-2.65, 9.4) * mm});
            skLineSegment(sketch, "E51.10.15", {"start": v(-2.65, 9.4) * mm, "end": v(-2.76, 9.54) * mm});
            skLineSegment(sketch, "E51.10.16", {"start": v(-4.77, 8.53) * mm, "end": v(-4.8, 8.7) * mm});
            skLineSegment(sketch, "E51.10.17", {"start": v(-4.74, 8.38) * mm, "end": v(-4.77, 8.53) * mm});
            skLineSegment(sketch, "E51.10.18", {"start": v(-4.8, 8.7) * mm, "end": v(-4.82, 8.9) * mm});
            skLineSegment(sketch, "E51.10.19", {"start": v(-2.46, 9.08) * mm, "end": v(-2.5, 9.17) * mm});
            skLineSegment(sketch, "E51.10.20", {"start": v(-2.42, 9) * mm, "end": v(-2.46, 9.08) * mm});
            skLineSegment(sketch, "E51.10.21", {"start": v(-4.71, 8.26) * mm, "end": v(-4.74, 8.38) * mm});
            skLineSegment(sketch, "E51.10.22", {"start": v(-4.68, 8.16) * mm, "end": v(-4.71, 8.26) * mm});
            skLineSegment(sketch, "E51.10.23", {"start": v(-4.63, 8.03) * mm, "end": v(-4.65, 8.08) * mm});
            skLineSegment(sketch, "E51.10.24", {"start": v(-2.39, 8.9) * mm, "end": v(-2.4, 8.92) * mm});
            skLineSegment(sketch, "E51.10.25", {"start": v(-2.4, 8.92) * mm, "end": v(-2.4, 8.95) * mm});
            skLineSegment(sketch, "E51.10.26", {"start": v(-4.65, 8.08) * mm, "end": v(-4.68, 8.16) * mm});
            skLineSegment(sketch, "E51.10.27", {"start": v(-2.4, 8.95) * mm, "end": v(-2.42, 9) * mm});
            skLineSegment(sketch, "E51.10.28", {"start": v(-4.62, 8) * mm, "end": v(-4.63, 8.03) * mm});
            skLineSegment(sketch, "E51.10.29", {"start": v(-4.61, 7.99) * mm, "end": v(-4.62, 8) * mm});
            skLineSegment(sketch, "E51.11.0", {"start": v(-6.66, 3.84) * mm, "end": v(-7.99, 4.61) * mm});
            skLineSegment(sketch, "E51.11.1", {"start": v(-7.78, 7.08) * mm, "end": v(-8.04, 7.14) * mm});
            skLineSegment(sketch, "E51.11.2", {"start": v(-5.44, 5.44) * mm, "end": v(-6.52, 6.52) * mm});
            skLineSegment(sketch, "E51.11.3", {"start": v(-7.55, 7.02) * mm, "end": v(-7.78, 7.08) * mm});
            skLineSegment(sketch, "E51.11.4", {"start": v(-8.74, 5.48) * mm, "end": v(-8.86, 5.69) * mm});
            skLineSegment(sketch, "E51.11.5", {"start": v(-8.86, 5.69) * mm, "end": v(-8.98, 5.92) * mm});
            skLineSegment(sketch, "E51.11.6", {"start": v(-7.34, 6.95) * mm, "end": v(-7.55, 7.02) * mm});
            skLineSegment(sketch, "E51.11.7", {"start": v(-8.33, 7.18) * mm, "end": v(-8.64, 7.22) * mm});
            skLineSegment(sketch, "E51.11.8", {"start": v(-7.16, 6.88) * mm, "end": v(-7.34, 6.95) * mm});
            skLineSegment(sketch, "E51.11.9", {"start": v(-9.1, 6.18) * mm, "end": v(-9.2, 6.47) * mm});
            skLineSegment(sketch, "E51.11.10", {"start": v(-8.04, 7.14) * mm, "end": v(-8.33, 7.18) * mm});
            skLineSegment(sketch, "E51.11.11", {"start": v(-8.62, 5.3) * mm, "end": v(-8.74, 5.48) * mm});
            skLineSegment(sketch, "E51.11.12", {"start": v(-8.98, 5.92) * mm, "end": v(-9.1, 6.18) * mm});
            skLineSegment(sketch, "E51.11.13", {"start": v(-6.76, 6.69) * mm, "end": v(-6.87, 6.75) * mm});
            skLineSegment(sketch, "E51.11.14", {"start": v(-6.87, 6.75) * mm, "end": v(-7, 6.82) * mm});
            skLineSegment(sketch, "E51.11.15", {"start": v(-7, 6.82) * mm, "end": v(-7.16, 6.88) * mm});
            skLineSegment(sketch, "E51.11.16", {"start": v(-8.4, 5) * mm, "end": v(-8.5, 5.13) * mm});
            skLineSegment(sketch, "E51.11.17", {"start": v(-8.3, 4.88) * mm, "end": v(-8.4, 5) * mm});
            skLineSegment(sketch, "E51.11.18", {"start": v(-8.5, 5.13) * mm, "end": v(-8.62, 5.3) * mm});
            skLineSegment(sketch, "E51.11.19", {"start": v(-6.67, 6.63) * mm, "end": v(-6.76, 6.69) * mm});
            skLineSegment(sketch, "E51.11.20", {"start": v(-6.6, 6.59) * mm, "end": v(-6.67, 6.63) * mm});
            skLineSegment(sketch, "E51.11.21", {"start": v(-8.2, 4.8) * mm, "end": v(-8.3, 4.88) * mm});
            skLineSegment(sketch, "E51.11.22", {"start": v(-8.13, 4.72) * mm, "end": v(-8.2, 4.8) * mm});
            skLineSegment(sketch, "E51.11.23", {"start": v(-8.02, 4.64) * mm, "end": v(-8.07, 4.67) * mm});
            skLineSegment(sketch, "E51.11.24", {"start": v(-6.52, 6.52) * mm, "end": v(-6.53, 6.53) * mm});
            skLineSegment(sketch, "E51.11.25", {"start": v(-6.53, 6.53) * mm, "end": v(-6.56, 6.55) * mm});
            skLineSegment(sketch, "E51.11.26", {"start": v(-8.07, 4.67) * mm, "end": v(-8.13, 4.72) * mm});
            skLineSegment(sketch, "E51.11.27", {"start": v(-6.56, 6.55) * mm, "end": v(-6.6, 6.59) * mm});
            skLineSegment(sketch, "E51.11.28", {"start": v(-8, 4.62) * mm, "end": v(-8.02, 4.64) * mm});
            skLineSegment(sketch, "E51.11.29", {"start": v(-7.99, 4.61) * mm, "end": v(-8, 4.62) * mm});
            skSolve(sketch);
        }
        {
            var Q0;
            {var subQ0=sQuery(id+"F1.wireOp",EDGE,"E0");var subQ27=makeQuery(id+"F1.imprint","INTERSECT",VERTEX,{"derivedFrom":[subQ0,sQuery(id+"F1.wireOp",EDGE,"E51.10.0")]});Q0=makeQuery(id+"F1.imprint","IMPRINT",FACE,{"disambiguationData":[TD([[makeQuery(id+"F1.imprint","IMPRINT",EDGE,{"disambiguationData":[TD([[subQ27,-1.0]])],"derivedFrom":subQ0}),1.0]])]});}
            var Q1;
            {var subQ0=sQuery(id+"F1.wireOp",EDGE,"E51.1.0");Q1=makeQuery(id+"F1.imprint","IMPRINT",FACE,{"disambiguationData":[TD([[makeQuery(id+"F1.imprint","IMPRINT",EDGE,{"derivedFrom":subQ0}),-1.0]])]});}
            var Q2;
            {var subQ7=sQuery(id+"F1.wireOp",EDGE,"E51.2.0");Q2=makeQuery(id+"F1.imprint","IMPRINT",FACE,{"disambiguationData":[TD([[makeQuery(id+"F1.imprint","IMPRINT",EDGE,{"derivedFrom":subQ7}),-1.0]])]});}
            var Q3;
            {var subQ8=sQuery(id+"F1.wireOp",EDGE,"E51.3.0");Q3=makeQuery(id+"F1.imprint","IMPRINT",FACE,{"disambiguationData":[TD([[makeQuery(id+"F1.imprint","IMPRINT",EDGE,{"derivedFrom":subQ8}),-1.0]])]});}
            var Q4;
            {var subQ2=sQuery(id+"F1.wireOp",EDGE,"E51.4.0");Q4=makeQuery(id+"F1.imprint","IMPRINT",FACE,{"disambiguationData":[TD([[makeQuery(id+"F1.imprint","IMPRINT",EDGE,{"derivedFrom":subQ2}),-1.0]])]});}
            var Q5;
            {var subQ8=sQuery(id+"F1.wireOp",EDGE,"E51.5.0");Q5=makeQuery(id+"F1.imprint","IMPRINT",FACE,{"disambiguationData":[TD([[makeQuery(id+"F1.imprint","IMPRINT",EDGE,{"derivedFrom":subQ8}),-1.0]])]});}
            var Q6;
            {var subQ3=sQuery(id+"F1.wireOp",EDGE,"E51.6.0");Q6=makeQuery(id+"F1.imprint","IMPRINT",FACE,{"disambiguationData":[TD([[makeQuery(id+"F1.imprint","IMPRINT",EDGE,{"derivedFrom":subQ3}),-1.0]])]});}
            var Q7;
            {var subQ0=sQuery(id+"F1.wireOp",EDGE,"E51.7.0");Q7=makeQuery(id+"F1.imprint","IMPRINT",FACE,{"disambiguationData":[TD([[makeQuery(id+"F1.imprint","IMPRINT",EDGE,{"derivedFrom":subQ0}),-1.0]])]});}
            var Q8;
            {var subQ5=sQuery(id+"F1.wireOp",EDGE,"E51.8.0");Q8=makeQuery(id+"F1.imprint","IMPRINT",FACE,{"disambiguationData":[TD([[makeQuery(id+"F1.imprint","IMPRINT",EDGE,{"derivedFrom":subQ5}),-1.0]])]});}
            var Q9;
            {var subQ1=sQuery(id+"F1.wireOp",EDGE,"E51.9.0");Q9=makeQuery(id+"F1.imprint","IMPRINT",FACE,{"disambiguationData":[TD([[makeQuery(id+"F1.imprint","IMPRINT",EDGE,{"derivedFrom":subQ1}),-1.0]])]});}
            var Q10;
            {var subQ5=sQuery(id+"F1.wireOp",EDGE,"E51.10.0");Q10=makeQuery(id+"F1.imprint","IMPRINT",FACE,{"disambiguationData":[TD([[makeQuery(id+"F1.imprint","IMPRINT",EDGE,{"derivedFrom":subQ5}),-1.0]])]});}
            var Q11;
            {var subQ8=sQuery(id+"F1.wireOp",EDGE,"E51.11.0");Q11=makeQuery(id+"F1.imprint","IMPRINT",FACE,{"disambiguationData":[TD([[makeQuery(id+"F1.imprint","IMPRINT",EDGE,{"derivedFrom":subQ8}),-1.0]])]});}
            var Q12;
            {var subQ2=sQuery(id+"F1.wireOp",EDGE,"E51.12.0");Q12=makeQuery(id+"F1.imprint","IMPRINT",FACE,{"disambiguationData":[TD([[makeQuery(id+"F1.imprint","IMPRINT",EDGE,{"derivedFrom":subQ2}),-1.0]])]});}
            var Q13;
            {var subQ3=sQuery(id+"F1.wireOp",EDGE,"E51.13.0");Q13=makeQuery(id+"F1.imprint","IMPRINT",FACE,{"disambiguationData":[TD([[makeQuery(id+"F1.imprint","IMPRINT",EDGE,{"derivedFrom":subQ3}),-1.0]])]});}
            var Q14;
            {var subQ0=sQuery(id+"F1.wireOp",EDGE,"E51.14.0");Q14=makeQuery(id+"F1.imprint","IMPRINT",FACE,{"disambiguationData":[TD([[makeQuery(id+"F1.imprint","IMPRINT",EDGE,{"derivedFrom":subQ0}),-1.0]])]});}
            var Q15;
            {var subQ6=sQuery(id+"F1.wireOp",EDGE,"E51.15.0");Q15=makeQuery(id+"F1.imprint","IMPRINT",FACE,{"disambiguationData":[TD([[makeQuery(id+"F1.imprint","IMPRINT",EDGE,{"derivedFrom":subQ6}),-1.0]])]});}
            var Q16;
            {var subQ5=sQuery(id+"F1.wireOp",EDGE,"E51.16.0");Q16=makeQuery(id+"F1.imprint","IMPRINT",FACE,{"disambiguationData":[TD([[makeQuery(id+"F1.imprint","IMPRINT",EDGE,{"derivedFrom":subQ5}),-1.0]])]});}
            var Q17;
            {var subQ7=sQuery(id+"F1.wireOp",EDGE,"E51.17.0");Q17=makeQuery(id+"F1.imprint","IMPRINT",FACE,{"disambiguationData":[TD([[makeQuery(id+"F1.imprint","IMPRINT",EDGE,{"derivedFrom":subQ7}),-1.0]])]});}
            var Q18;
            {var subQ5=sQuery(id+"F1.wireOp",EDGE,"E51.18.0");Q18=makeQuery(id+"F1.imprint","IMPRINT",FACE,{"disambiguationData":[TD([[makeQuery(id+"F1.imprint","IMPRINT",EDGE,{"derivedFrom":subQ5}),-1.0]])]});}
            var Q19;
            {var subQ8=sQuery(id+"F1.wireOp",EDGE,"E51.19.0");Q19=makeQuery(id+"F1.imprint","IMPRINT",FACE,{"disambiguationData":[TD([[makeQuery(id+"F1.imprint","IMPRINT",EDGE,{"derivedFrom":subQ8}),-1.0]])]});}
            var Q20;
            {var subQ8=sQuery(id+"F1.wireOp",EDGE,"E21");Q20=makeQuery(id+"F1.imprint","IMPRINT",FACE,{"disambiguationData":[TD([[makeQuery(id+"F1.imprint","IMPRINT",EDGE,{"derivedFrom":subQ8}),-1.0]])]});}
            extrude(context, id + "F2", {"entities" : qUnion([Q0, Q1, Q2, Q3, Q4, Q5, Q6, Q7, Q8, Q9, Q10, Q11, Q12, Q13, Q14, Q15, Q16, Q17, Q18, Q19, Q20]), "depth" : (getVariable(context, 'GearThickness')) * mm, "offsetDistance" : 25 * mm});
        }
    });
